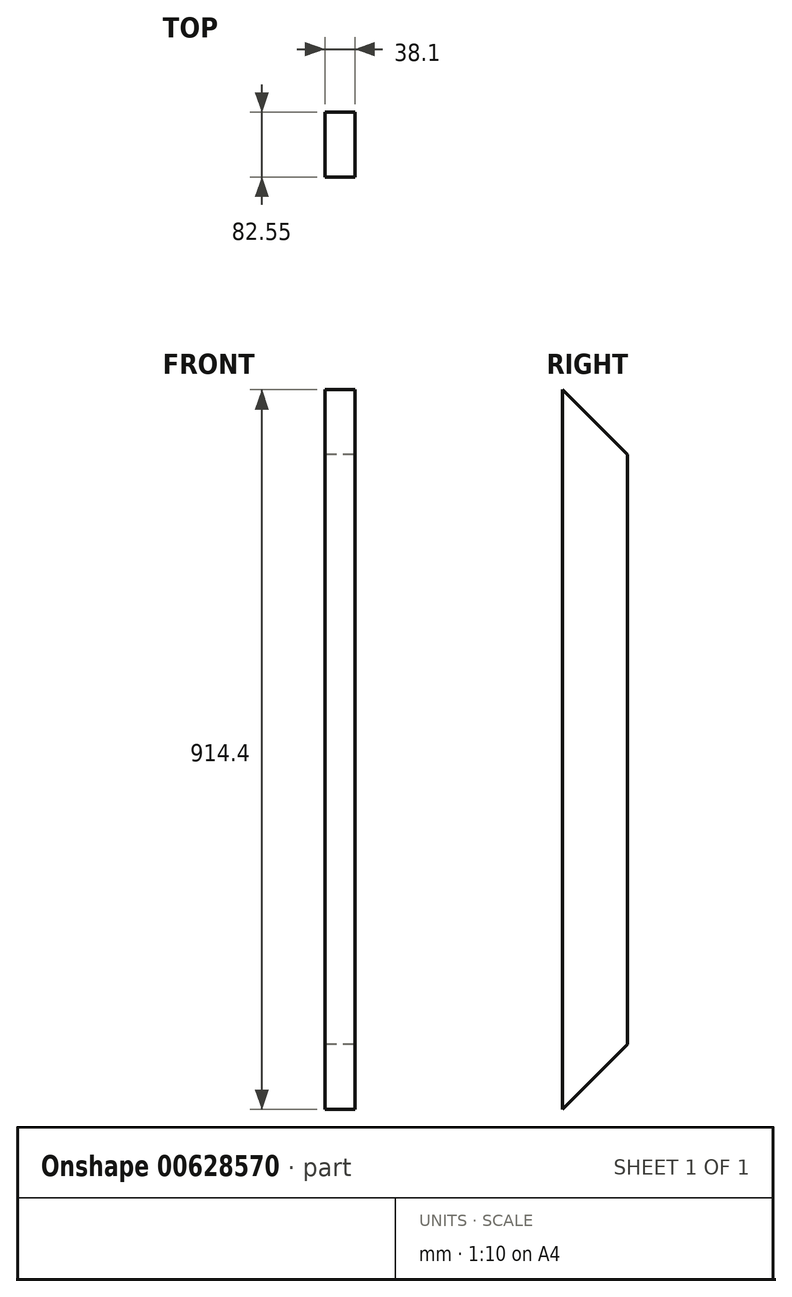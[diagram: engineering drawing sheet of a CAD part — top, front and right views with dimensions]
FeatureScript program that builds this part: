
annotation { "Feature Type Name" : "Feature", "Feature Type Description" : "" }
export const myFeature = defineFeature(function(context is Context, id is Id, definition is map)
    precondition{}
    {
        {
            var Q0;
            Q0=qCreatedBy(makeId("Right.planeOp"),FACE);
            var sketch = newSketch(context, id + "F0", { "sketchPlane" : qUnion([Q0])});
            skLineSegment(sketch, "E0", {"start": v(0, 0) * mm, "end": v(0, -457.2) * mm});
            skLineSegment(sketch, "E1", {"start": v(0, -457.2) * mm, "end": v(0, 457.2) * mm});
            skLineSegment(sketch, "E2", {"start": v(0, 457.2) * mm, "end": v(82.55, 374.65) * mm});
            skLineSegment(sketch, "E3", {"start": v(82.55, 374.65) * mm, "end": v(82.55, -374.65) * mm});
            skLineSegment(sketch, "E4", {"start": v(82.55, -374.65) * mm, "end": v(0, -457.2) * mm});
            skSolve(sketch);
        }
        {
            var Q0;
            Q0 = qSketchRegion(id + "F0", true);
            extrude(context, id + "F1", {"entities" : qUnion([Q0]), "endBound" : BoundingType.SYMMETRIC, "depth" : 38.1 * mm, "offsetDistance" : 25.4 * mm});
        }
    });
